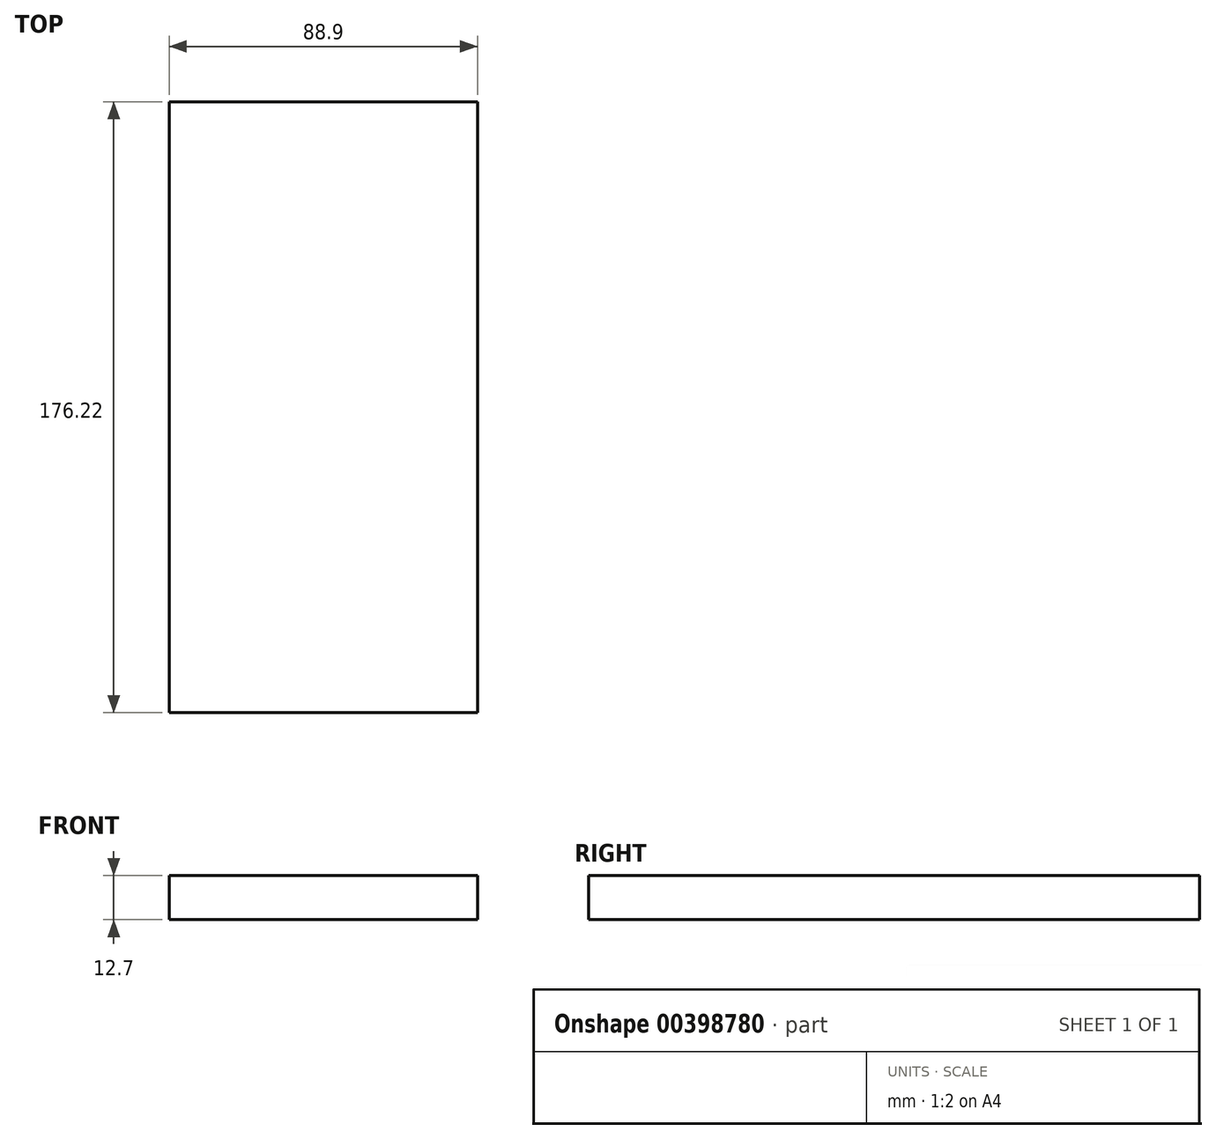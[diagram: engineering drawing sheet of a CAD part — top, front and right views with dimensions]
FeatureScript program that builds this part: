
annotation { "Feature Type Name" : "Feature", "Feature Type Description" : "" }
export const myFeature = defineFeature(function(context is Context, id is Id, definition is map)
    precondition{}
    {
        {
            var Q0;
            Q0=qCreatedBy(makeId("Front.planeOp"),FACE);
            var sketch = newSketch(context, id + "F0", { "sketchPlane" : qUnion([Q0])});
            skLineSegment(sketch, "E0.bottom", {"start": v(-44.45, 6.35) * mm, "end": v(44.45, 6.35) * mm});
            skLineSegment(sketch, "E0.top", {"start": v(-44.45, -6.35) * mm, "end": v(44.45, -6.35) * mm});
            skLineSegment(sketch, "E0.left", {"start": v(-44.45, 6.35) * mm, "end": v(-44.45, -6.35) * mm});
            skLineSegment(sketch, "E0.right", {"start": v(44.45, 6.35) * mm, "end": v(44.45, -6.35) * mm});
            skLineSegment(sketch, "E1", {"start": v(0, 6.35) * mm, "end": v(0, -6.35) * mm, "construction": true});
            skSolve(sketch);
        }
        {
            var Q0;
            Q0=makeQuery(id+"F0.imprint","IMPRINT",FACE,{"disambiguationData":[TD([[makeQuery(id+"F0.imprint","IMPRINT",EDGE,{"derivedFrom":sQuery(id+"F0.wireOp",EDGE,"E0.bottom")}),-1.0]])]});
            extrude(context, id + "F1", {"entities" : qUnion([Q0]), "endBound" : BoundingType.SYMMETRIC, "depth" : 176.21 * mm});
        }
    });
